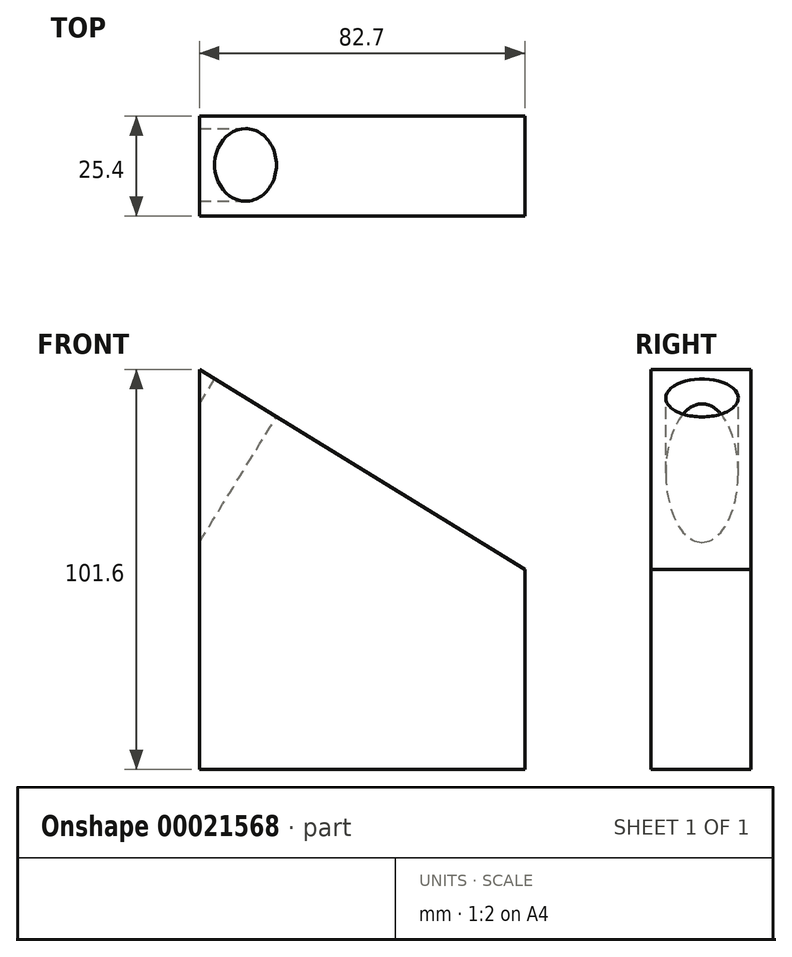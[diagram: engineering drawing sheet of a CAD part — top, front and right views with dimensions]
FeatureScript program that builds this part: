
annotation { "Feature Type Name" : "Feature", "Feature Type Description" : "" }
export const myFeature = defineFeature(function(context is Context, id is Id, definition is map)
    precondition{}
    {
        {
            var Q0;
            Q0=qCreatedBy(makeId("Front.planeOp"),FACE);
            var sketch = newSketch(context, id + "F0", { "sketchPlane" : qUnion([Q0])});
            skLineSegment(sketch, "E0.rect.bottom", {"start": v(-41.35, 25.4) * mm, "end": v(41.35, 25.4) * mm});
            skLineSegment(sketch, "E0.rect.top", {"start": v(-41.35, -25.4) * mm, "end": v(41.35, -25.4) * mm});
            skLineSegment(sketch, "E0.rect.left", {"start": v(-41.35, 25.4) * mm, "end": v(-41.35, -25.4) * mm});
            skLineSegment(sketch, "E0.rect.right", {"start": v(41.35, 25.4) * mm, "end": v(41.35, -25.4) * mm});
            skPoint(sketch, "E0.rect.middle", {"position": v(0, 0) * mm});
            skLineSegment(sketch, "E1", {"start": v(-41.35, 25.4) * mm, "end": v(-41.35, 76.2) * mm});
            skLineSegment(sketch, "E2", {"start": v(-41.35, 76.2) * mm, "end": v(41.35, 25.4) * mm});
            skSolve(sketch);
        }
        {
            var Q0;
            Q0 = qSketchRegion(id + "F0", true);
            extrude(context, id + "F1", {"entities" : qUnion([Q0]), "depth" : 25.4 * mm});
        }
        {
            var Q0;
            Q0=makeQuery(id+"F1.opExtrude","SWEPT_FACE",FACE,{"disambiguationData":[OSD([sQuery(id+"F0.wireOp",EDGE,"E2")])]});
            var sketch = newSketch(context, id + "F2", { "sketchPlane" : qUnion([Q0])});
            skCircle(sketch, "E3", {"center": v(-61.35, -12.4) * mm, "radius": 9.2 * mm});
            skLineSegment(sketch, "E4", {"start": v(-61.35, -12.4) * mm, "end": v(21.95, -12.4) * mm});
            skCircle(sketch, "E5", {"center": v(-32.83, -12.4) * mm, "radius": 10.8 * mm});
            skSolve(sketch);
        }
        {
            var Q0;
            Q0=sQuery(id+"F2.wireOp",VERTEX,"E3.center");
            var Q1;
            Q1=makeQuery(id+"F1.opExtrude","SWEPT_BODY",BODY,{"disambiguationData":[OSD([sQuery(id+"F0.wireOp",EDGE,"E0.rect.top"),sQuery(id+"F0.wireOp",EDGE,"E0.rect.left"),sQuery(id+"F0.wireOp",EDGE,"E0.rect.right"),sQuery(id+"F0.wireOp",EDGE,"E1"),sQuery(id+"F0.wireOp",EDGE,"E2")])]});
            hole(context, id + "F3", {"style" : HoleStyle.SIMPLE, "holeDiameter" : 18.41 * mm, "endStyle" : HoleEndStyle.THROUGH, "locations" : qUnion([Q0]), "scope" : qUnion([Q1])});
        }
    });
